# Revit family: Hand_Wash_Trough-3_Station-Acorn-SWS060_Series
name_source: partatom
category: Plumbing Fixtures
units: mm (PartAtom-declared; Revit-internal decimal feet)

## family parameters
Cut with Voids When Loaded = No
Host = Face
OmniClass Number = 23.45.05.14.14
OmniClass Title = Sinks/Lavatories
Part Type = Normal
Room Calculation Point = No
Round Connector Dimension = Use Diameter
Shared = Yes

## types (3) — shared parameters
Assembly Code = D2010440
Backsplash Height = 10"
Bowl Depth = 16 1/2"
Bowl Height = 8"
Bowl Width = 57"
CW Connection = No
Default Elevation = 34"
Depth = 20"
Description = 60" wide 3 user hand wash trough
Drain Opening Size = 3 1/2"
Faucet Hole Diameter = 1 1/2"
Finish = Stainless Steel-Acorn-Polished Satin
HW Connection = No
Height = 18"
Installation Type = Wall Mounted
Manufacturer = Acorn Engineering
Material = Stainless Steel-Acorn-Polished Satin
Shipping Weight = 90 lbs (41 kg)
Type Comments = Wall hung Hand Wash Trough
URL = https://acorneng.com
Vent Connection = No
Waste Connection = No
Width = 60"
cUPC Compliant = Yes
zero-valued in all types: CWFU, HWFU, WFU

## per-type parameters (varying)
| type | 8" Centers Distance | H0-No Faucet Punching | H1-Single Hole Centered | H28-2 Holes on 8" Centers | Single Center Distance |
| SWS060-H0 | 1" | Yes | No | No | 1" |
| SWS060-H1 | 1" | No | Yes | No | 3" |
| SWS060-H28 | 3" | No | No | Yes | 1" |

note: column(s) folded — value = type name in every type: Model

## geometry (parser evidence)
native form markers: Sweep x3
no freeform markers — native parametric forms only
